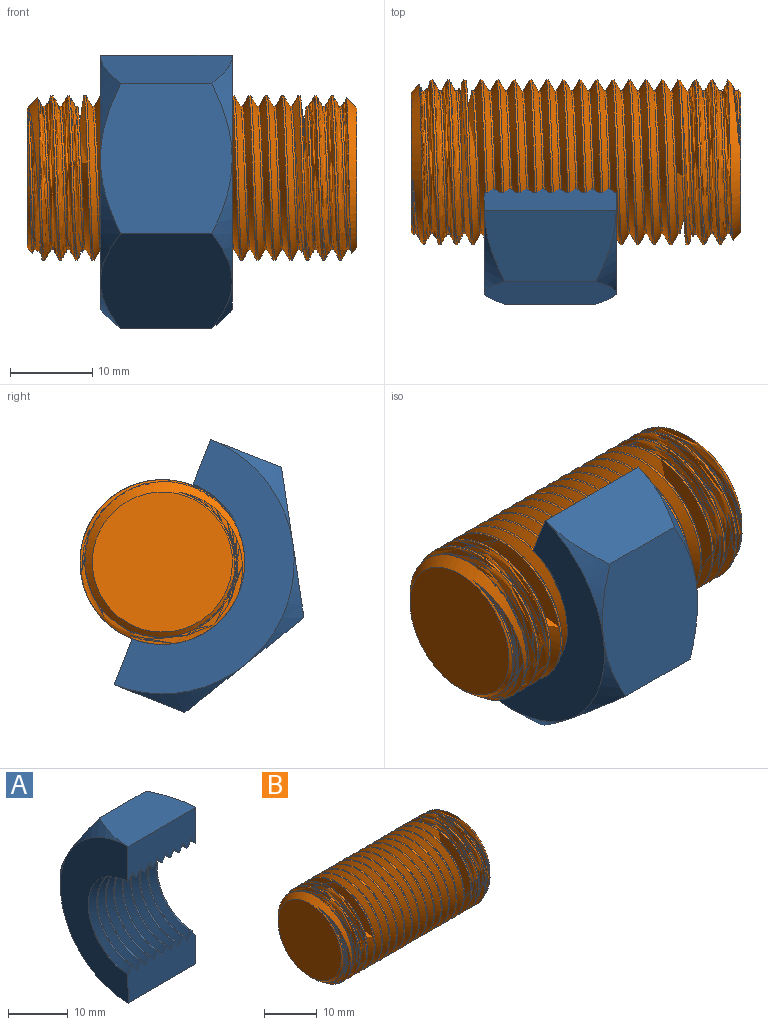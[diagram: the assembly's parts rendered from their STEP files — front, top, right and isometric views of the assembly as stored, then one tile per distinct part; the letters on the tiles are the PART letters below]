
ASSEMBLY  parts=2 mates=1
PART A: 49 faces, bbox 18.7x28.2x37.9 mm
  f0: plane 16x7.23mm, normal (0,-1,0), area 105.3mm2, adj f9,f11,f12,f13,f14,f15,f16,f17
  f1: cone r=18.5mm half-angle=45deg, axis (-1,0,0), area 19.5mm2, adj f2,f4,f47
  f2: plane 16.01x16mm, normal (0,0.87,-0.5), area 264.2mm2, adj f1,f3,f4,f6,f7,f8
  f3: cone r=18.5mm half-angle=45deg, axis (-1,0,0), area 19.5mm2, adj f2,f6,f47
  f4: plane 16.01x16mm, normal (0,0.87,0.5), area 264.2mm2, adj f1,f2,f5,f8,f9,f10
  f5: cone r=18.5mm half-angle=45deg, axis (-1,0,0), area 19.5mm2, adj f4,f9,f47
  f6: plane 16.01x9.24mm, normal (0,0,-1), area 132.1mm2, adj f2,f3,f7,f48
  f7: cone r=18.5mm half-angle=45deg, axis (1,0,0), area 19.5mm2, adj f2,f6,f46
  f8: cone r=18.5mm half-angle=45deg, axis (1,0,0), area 19.5mm2, adj f2,f4,f46
  f9: plane 16.01x9.24mm, normal (0,0,1), area 132.1mm2, adj f0,f4,f5,f10
  f10: cone r=18.5mm half-angle=45deg, axis (1,0,0), area 19.5mm2, adj f4,f9,f46
  f11: cylinder r=8.77mm len=17.53mm, axis (-1,0,0), area 7.2mm2, adj f0,f12,f19,f48
  f12: bspline ~20.54x20.33mm, area 48.1mm2, adj f0,f11,f13,f48
  f13: cylinder r=10.17mm len=20.33mm, axis (-1,0,0), area 3.9mm2, adj f0,f12,f15,f46,f48
  f14: cylinder r=8.77mm len=3.52mm, axis (-1,0,0), area 0.2mm2, adj f0,f15,f46
  f15: bspline ~20.54x20.33mm, area 26.1mm2, adj f0,f13,f14,f46
  f16: cylinder r=8.77mm len=17.53mm, axis (-1,0,0), area 7.2mm2, adj f0,f17,f23,f48
  f17: bspline ~20.54x20.33mm, area 48.1mm2, adj f0,f16,f18,f48
  f18: cylinder r=10.17mm len=20.33mm, axis (-1,0,0), area 4mm2, adj f0,f17,f19,f48
  f19: bspline ~20.54x20.33mm, area 48.1mm2, adj f0,f11,f18,f48
  f20: cylinder r=8.77mm len=17.53mm, axis (-1,0,0), area 7.2mm2, adj f0,f21,f27,f48
  f21: bspline ~20.54x20.33mm, area 48.1mm2, adj f0,f20,f22,f48
  f22: cylinder r=10.17mm len=20.33mm, axis (-1,0,0), area 4mm2, adj f0,f21,f23,f48
  f23: bspline ~20.54x20.33mm, area 48.1mm2, adj f0,f16,f22,f48
  f24: cylinder r=8.77mm len=17.53mm, axis (-1,0,0), area 7.2mm2, adj f0,f25,f31,f48
  f25: bspline ~20.54x20.33mm, area 48.1mm2, adj f0,f24,f26,f48
  f26: cylinder r=10.17mm len=20.33mm, axis (-1,0,0), area 4mm2, adj f0,f25,f27,f48
  f27: bspline ~20.54x20.33mm, area 48.1mm2, adj f0,f20,f26,f48
  f28: cylinder r=8.77mm len=17.53mm, axis (-1,0,0), area 7.2mm2, adj f0,f29,f35,f48
  f29: bspline ~20.54x20.33mm, area 48.1mm2, adj f0,f28,f30,f48
  f30: cylinder r=10.17mm len=20.33mm, axis (-1,0,0), area 4mm2, adj f0,f29,f31,f48
  f31: bspline ~20.54x20.33mm, area 48.1mm2, adj f0,f24,f30,f48
  f32: cylinder r=8.77mm len=17.53mm, axis (-1,0,0), area 7.2mm2, adj f0,f33,f39,f48
  f33: bspline ~20.54x20.33mm, area 48.1mm2, adj f0,f32,f34,f48
  f34: cylinder r=10.17mm len=20.33mm, axis (-1,0,0), area 4mm2, adj f0,f33,f35,f48
  f35: bspline ~20.54x20.33mm, area 48.1mm2, adj f0,f28,f34,f48
  f36: cylinder r=8.77mm len=17.53mm, axis (-1,0,0), area 7.2mm2, adj f0,f37,f43,f48
  f37: bspline ~20.54x20.33mm, area 48.1mm2, adj f0,f36,f38,f48
  f38: cylinder r=10.17mm len=20.33mm, axis (-1,0,0), area 4mm2, adj f0,f37,f39,f48
  f39: bspline ~20.54x20.33mm, area 48.1mm2, adj f0,f32,f38,f48
  f40: cylinder r=8.77mm len=17.53mm, axis (-1,0,0), area 6.9mm2, adj f0,f41,f45,f47,f48
  f41: bspline ~20.54x20.33mm, area 48.1mm2, adj f0,f40,f42,f48
  f42: cylinder r=10.17mm len=20.33mm, axis (-1,0,0), area 4mm2, adj f0,f41,f43,f48
  f43: bspline ~20.54x20.33mm, area 48.1mm2, adj f0,f36,f42,f48
  f44: cylinder r=10.17mm len=2.08mm, axis (-1,0,0), area 0.1mm2, adj f45,f47,f48
  f45: bspline ~20.33x11.74mm, area 22mm2, adj f40,f44,f47,f48
  f46: plane 32.92x16.92mm, normal (-1,0,0), area 262.4mm2, adj f0,f7,f8,f10,f13,f14,f15,f48
  f47: plane 32.92x16.92mm, normal (1,0,0), area 262.4mm2, adj f0,f1,f3,f5,f40,f44,f45,f48
  f48: plane 16x7.23mm, normal (0,-1,0), area 105.3mm2, adj f6,f11,f12,f13,f16,f17,f18,f19
PART B: 8 faces, bbox 41.8x23.1x20 mm
  f0: plane 17x17mm, normal (1,0,0), area 227mm2, adj f3
  f1: cylinder r=10mm len=37mm, axis (-1,0,0), area 568.4mm2, adj f3,f4,f5,f7
  f2: plane 17x17mm, normal (-1,0,0), area 227mm2, adj f4
  f3: cone r=10mm half-angle=45deg, axis (-1,0,0), area 68.4mm2, adj f0,f1,f5,f6,f7
  f4: cone r=8.5mm half-angle=45deg, axis (1,0,0), area 68.4mm2, adj f1,f2,f5,f6,f7
  f5: bspline ~40.75x23.09mm, area 1706.6mm2, adj f1,f3,f4,f6
  f6: cylinder r=8.7mm len=39.6mm, axis (-1,0,0), area 259.2mm2, adj f3,f4,f5,f7
  f7: bspline ~40.75x23.09mm, area 1686.1mm2, adj f1,f3,f4,f6
PLACE A rot(axis=(-1,0,0),158.5deg) t=(-12.56,-3.23,6.79)mm
PLACE B t=(-9.44,-3.23,6.79)mm fixed
MATE cylindrical A.f1 <-> B.f1  axis (1,0,0) through (-4.56,-3.23,6.79)mm
